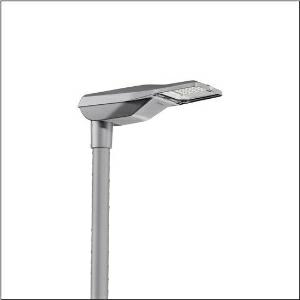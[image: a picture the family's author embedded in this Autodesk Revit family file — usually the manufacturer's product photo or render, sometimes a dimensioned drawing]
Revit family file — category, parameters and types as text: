
# Revit family: streetlight_sl_21_iq_micro___st1_0ab_5xe1m31g08db_d575
name_source: partatom
category: Lighting Fixtures
units: mm (PartAtom-declared; Revit-internal decimal feet)

## family parameters
Cut with Voids When Loaded = No
Host = Face
Light Source = No
Part Type = Normal
Room Calculation Point = No
Round Connector Dimension = Use Diameter
Shared = No

## types (1)
- --- (1 x LED, 4240 lm, 36.4 W, 3000K)
    Apparent Load = 36 VA
    CIE Flux Codes = 38 73 97 100 100
    Color Rendering = 70
    Color Temperature = 3000K
    Default Elevation = 1800 mm
    Description = Streetlight SL 21 iQ micro, mast luminaire, primary light control with lens, of PMMA, primary optical cover: cover, of toughened safety glass, transparent, light distribution: ST1.0aB, light emission: direct distribution, primary light characteristic: asymmetric, installation type: post-top, side-entry, LED, High Power LED, rated luminous flux: 4.240lm, luminous efficacy: 117lm/W, light colour: 730, colour temperature: 3000K, control gear: iQ Street-Remote, control: Street-Remote, Auto-Match, Temp-Guard, Lumen-Switch, Night-Set, Smart-Wire, Light-Fading, Desk-Remote (wireless, voltage-free reading and setting of iQ features in the workshop via application-optimized NFC function/RFID function), optimised constant luminous flux control (CLO 2.0), pre-setting: linear dimming characteristic, mains connection: 220..240V, AC, 50/60Hz, start of lifetime: 36W, end of service life: 38W, reduction: 16W, luminaire housing, of diecast aluminium, powder-coated, Siteco® metallic grey (DB 702S), corrosivity category C5 mid according to DIN EN ISO 12944, please order mast flange separately, inclination adjustable: 0°, 5°, 10°, 15°, sealing non-destructively replaceable, multi-level sealing system, length: 528mm, width: 235mm, height: 110mm, mast flange for spigot size: 42mm (side-entry): 5XC10008XM4, 60/48mm (side-entry/post-top): 5XC10108XM2, 76/60mm (side-entry/post-top): 5XC10108XM1, protection rating (complete): IP66, insulation class (complete): insulation class II (safety insulation), certification: CE, ENEC, ENEC+, VDE, impact resistance: IK10, permissible operating ambient temperature for outdoor applications: -40..+50°C, standard-compliant lighting for roads and squares, packaging unit: 1 piece

Light Distribution: ST1.0aB
    Height = 110 mm
    Lamp = 1 x LED
    Lamp Light Flux = 4240 lm
    Lamp Power = 36.4 W
    Lamp count = 1
    Length = 528 mm
    Luminous efficacy = 116 lm/W
    Manufacturer = Siteco
    ModVariant = No
    Model = 5XE1M31G08DB
    Number of Poles = 1
    OnlyDefault = Yes
    Power Factor = 1
    Product Name = Streetlight SL 21 iQ micro | ST1.0aB
    Product group = mast luminaire | pylon top
    ProductGroupID = 6100
    Protection Class = Protection class II
    Protection Degree = IP 66
    RLX_Detail_Level = 1
    RLX_Emergency_Light_Flux = 0 lm
    RLX_Emergency_Type = 0
    RLX_Emergency_Type_DB = No
    RlxData = <blob elided: 99037 chars, md5=01e8742a>
    Socket = socket
    Standby Power = 0 W
    System Light Flux = 4240 lm
    System Power = 36 W
    Type Comments = factory setting: luminous flux: 100 % | dim-lin: 254 | 715 mA
    Type Image = l_1006881.jpg
    URL = http://relux.com
    VarID = @adj_154092
    Voltage = 0 V
    Weight = 0.00 kg
    Width = 235 mm

## geometry (parser evidence)
native form markers: Blend x4, Sweep x10
no freeform markers — native parametric forms only
